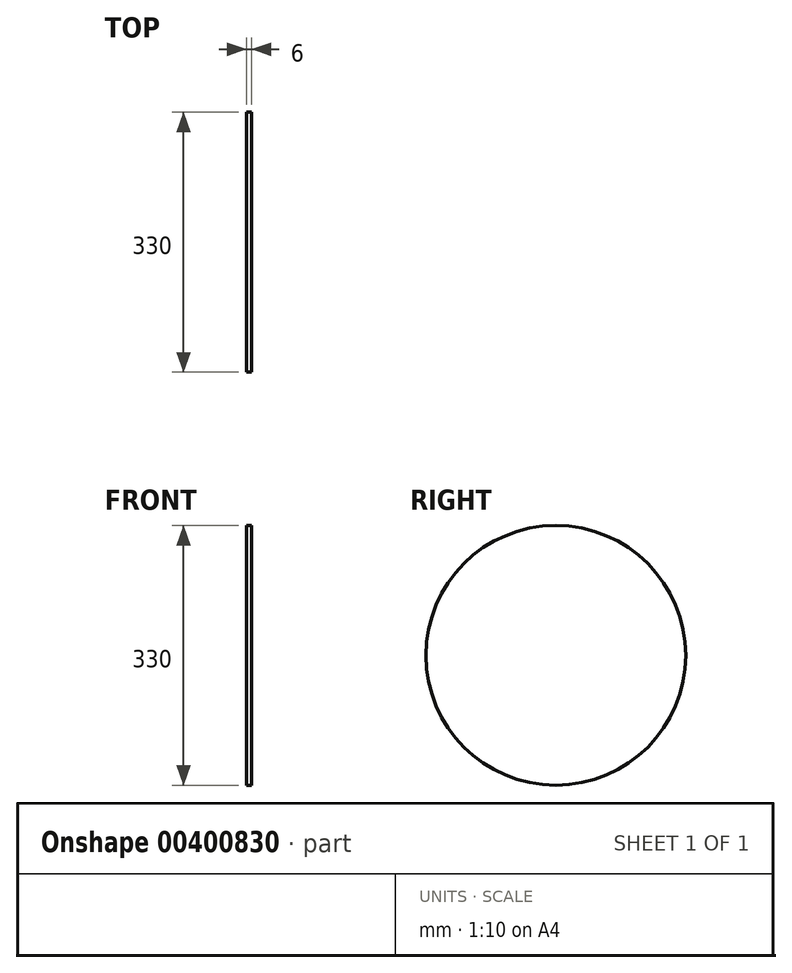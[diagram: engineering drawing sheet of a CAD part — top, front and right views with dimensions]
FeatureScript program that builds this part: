
annotation { "Feature Type Name" : "Feature", "Feature Type Description" : "" }
export const myFeature = defineFeature(function(context is Context, id is Id, definition is map)
    precondition{}
    {
        {
            var Q0;
            Q0=qCreatedBy(makeId("Right.planeOp"),FACE);
            var sketch = newSketch(context, id + "F0", { "sketchPlane" : qUnion([Q0])});
            skCircle(sketch, "E0", {"center": v(0, 0) * mm, "radius": 165 * mm});
            skSolve(sketch);
        }
        {
            var Q0;
            Q0=makeQuery(id+"F0.imprint","IMPRINT",FACE,{"disambiguationData":[TD([[makeQuery(id+"F0.imprint","IMPRINT",EDGE,{"derivedFrom":sQuery(id+"F0.wireOp",EDGE,"E0")}),1.0]])]});
            extrude(context, id + "F1", {"entities" : qUnion([Q0]), "depth" : 6 * mm});
        }
    });
